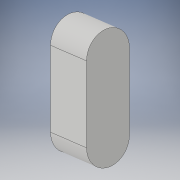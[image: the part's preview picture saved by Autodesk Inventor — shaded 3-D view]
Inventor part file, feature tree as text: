
AUTODESK INVENTOR PART (.ipt)
format: ipt  version: 2018 (Build 220112000, 112)  size: 94,720 bytes
history: native  units: mm
features: extrude x1, sketch x1
ambient origin geometry x8: Origin, YZ Plane, XZ Plane, XY Plane, X Axis, Y Axis, Z Axis, Center Point
bodies: Solid1 (feature_tree)
feature tree (2):
  extrude  "Extrusion1"  Depth=3.0mm
  sketch  "Sketch1"  dims[d0=1.5mm d1=5.0mm d2=3.0mm d3=0.0mm]
